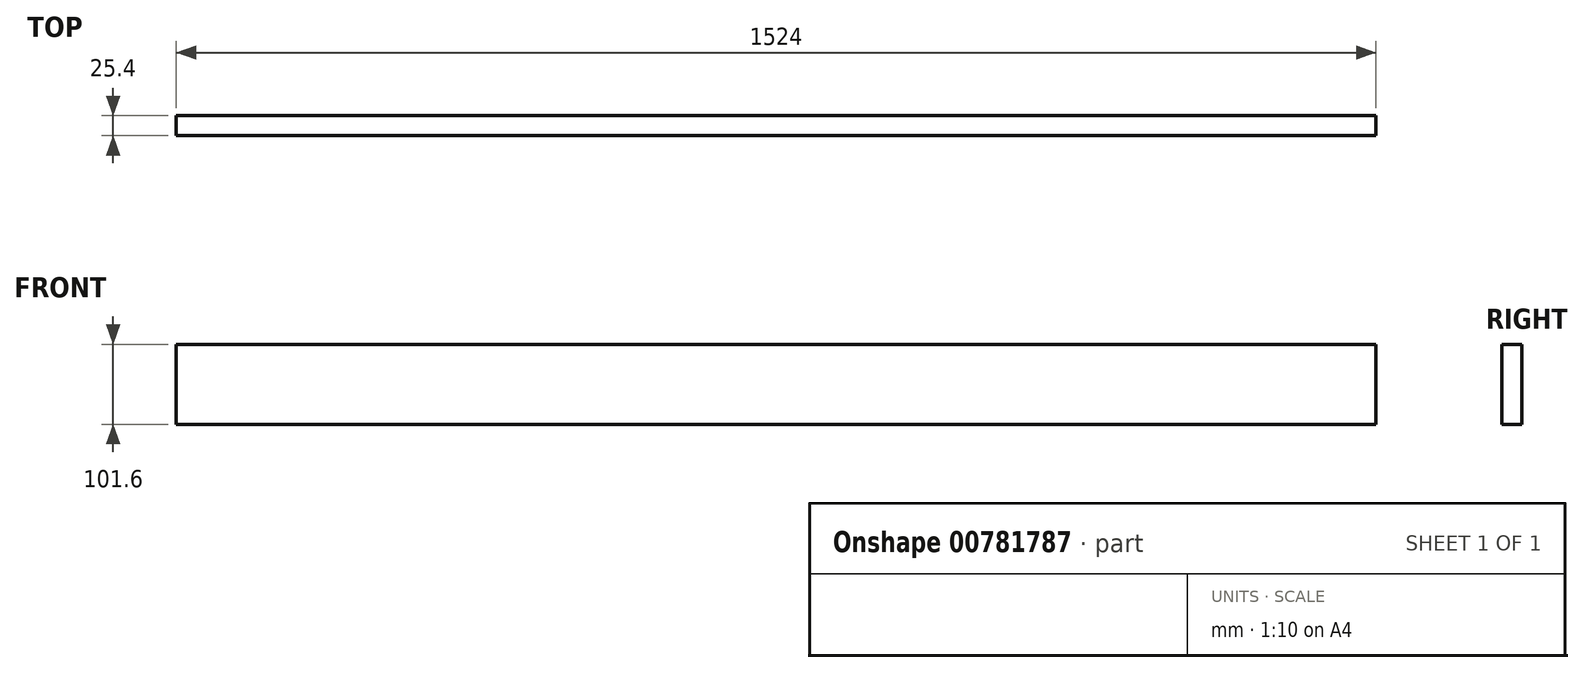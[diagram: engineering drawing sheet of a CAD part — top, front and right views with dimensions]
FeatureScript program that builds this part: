
annotation { "Feature Type Name" : "Feature", "Feature Type Description" : "" }
export const myFeature = defineFeature(function(context is Context, id is Id, definition is map)
    precondition{}
    {
        {
            var Q0;
            Q0=qCreatedBy(makeId("Front.planeOp"),FACE);
            var sketch = newSketch(context, id + "F0", { "sketchPlane" : qUnion([Q0])});
            skLineSegment(sketch, "E0.bottom", {"start": v(-757.98, -85.63) * mm, "end": v(766.02, -85.63) * mm});
            skLineSegment(sketch, "E0.top", {"start": v(-757.98, -187.23) * mm, "end": v(766.02, -187.23) * mm});
            skLineSegment(sketch, "E0.left", {"start": v(-757.98, -85.63) * mm, "end": v(-757.98, -187.23) * mm});
            skLineSegment(sketch, "E0.right", {"start": v(766.02, -85.63) * mm, "end": v(766.02, -187.23) * mm});
            skSolve(sketch);
        }
        {
            var Q0;
            Q0=makeQuery(id+"F0.imprint","IMPRINT",FACE,{"disambiguationData":[TD([[makeQuery(id+"F0.imprint","IMPRINT",EDGE,{"derivedFrom":sQuery(id+"F0.wireOp",EDGE,"E0.bottom")}),-1.0]])]});
            extrude(context, id + "F1", {"entities" : qUnion([Q0]), "depth" : 25.4 * mm, "offsetDistance" : 25.4 * mm});
        }
    });
